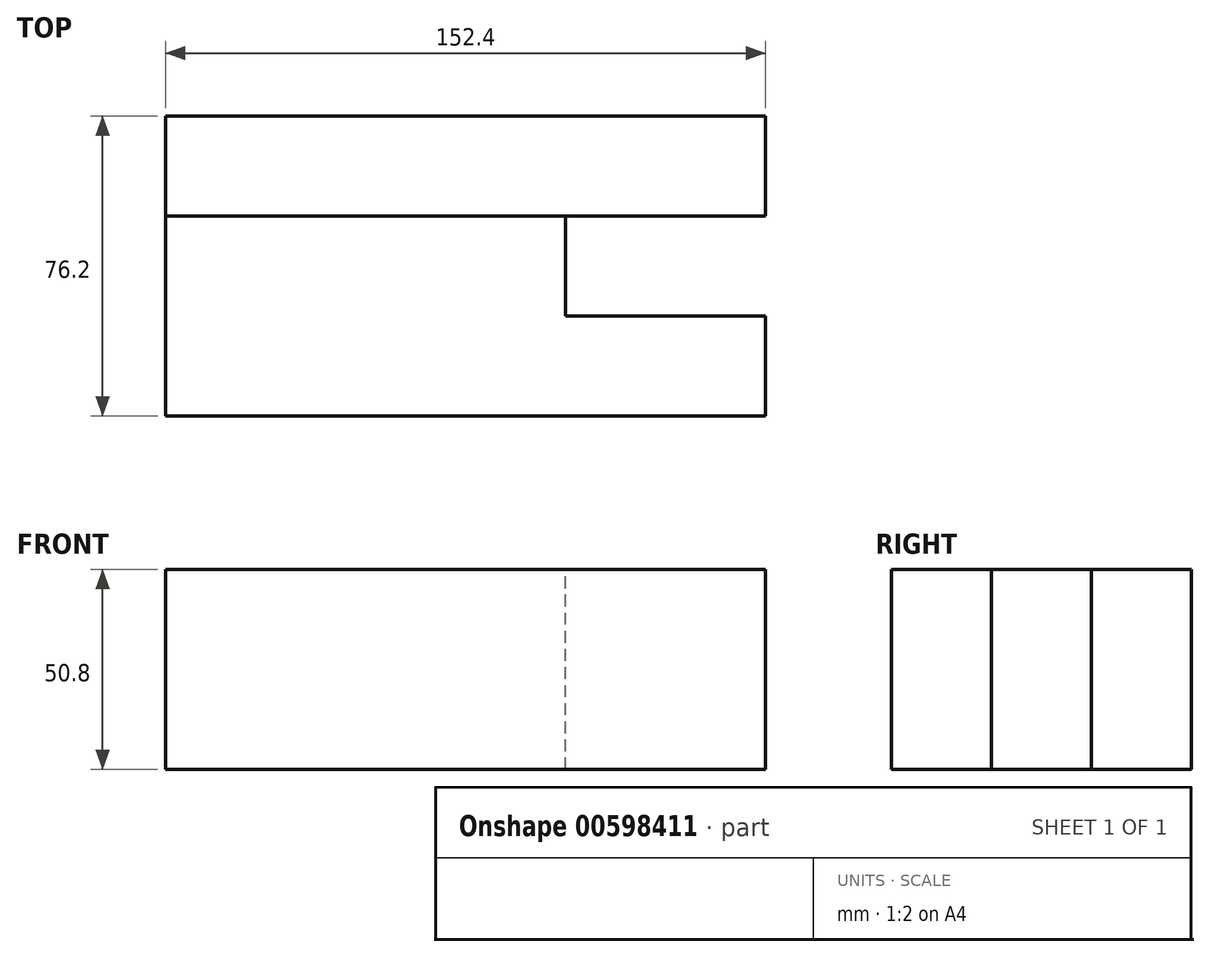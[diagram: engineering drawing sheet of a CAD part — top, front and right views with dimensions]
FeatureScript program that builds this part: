
annotation { "Feature Type Name" : "Feature", "Feature Type Description" : "" }
export const myFeature = defineFeature(function(context is Context, id is Id, definition is map)
    precondition{}
    {
        {
            var Q0;
            Q0=qCreatedBy(makeId("Front.planeOp"),FACE);
            var sketch = newSketch(context, id + "F0", { "sketchPlane" : qUnion([Q0])});
            skLineSegment(sketch, "E0", {"start": v(0, 0) * mm, "end": v(0, 50.8) * mm});
            skLineSegment(sketch, "E1", {"start": v(0, 50.8) * mm, "end": v(152.4, 50.8) * mm});
            skLineSegment(sketch, "E2", {"start": v(0, 0) * mm, "end": v(152.4, 0) * mm});
            skLineSegment(sketch, "E3", {"start": v(152.4, 50.8) * mm, "end": v(152.4, 0) * mm});
            skSolve(sketch);
        }
        {
            var Q0;
            Q0 = qSketchRegion(id + "F0", true);
            extrude(context, id + "F1", {"entities" : qUnion([Q0]), "depth" : 25.4 * mm, "offsetDistance" : 25.4 * mm});
        }
        {
            var Q0;
            Q0=qCreatedBy(makeId("Right.planeOp"),FACE);
            var sketch = newSketch(context, id + "F2", { "sketchPlane" : qUnion([Q0])});
            skLineSegment(sketch, "E4", {"start": v(0, 0) * mm, "end": v(0, 50.8) * mm});
            skLineSegment(sketch, "E5", {"start": v(0, 50.8) * mm, "end": v(25.4, 50.8) * mm});
            skLineSegment(sketch, "E6", {"start": v(25.4, 50.8) * mm, "end": v(25.4, 0) * mm});
            skLineSegment(sketch, "E7", {"start": v(25.4, 0) * mm, "end": v(0, 0) * mm});
            skSolve(sketch);
        }
        {
            var Q0;
            Q0 = qSketchRegion(id + "F2", true);
            extrude(context, id + "F3", {"entities" : qUnion([Q0]), "operationType" : NewBodyOperationType.ADD, "depth" : 101.6 * mm, "offsetDistance" : 25.4 * mm});
        }
        {
            var Q0;
            Q0=qCreatedBy(makeId("Right.planeOp"),FACE);
            var sketch = newSketch(context, id + "F4", { "sketchPlane" : qUnion([Q0])});
            skLineSegment(sketch, "E8", {"start": v(25.4, 0) * mm, "end": v(50.8, 0) * mm});
            skLineSegment(sketch, "E9", {"start": v(50.8, 0) * mm, "end": v(50.8, 50.8) * mm});
            skLineSegment(sketch, "E10", {"start": v(50.8, 50.8) * mm, "end": v(25.4, 50.8) * mm});
            skLineSegment(sketch, "E11", {"start": v(25.4, 50.8) * mm, "end": v(25.4, 0) * mm});
            skSolve(sketch);
        }
        {
            var Q0;
            Q0 = qSketchRegion(id + "F4", true);
            extrude(context, id + "F5", {"entities" : qUnion([Q0]), "depth" : 152.4 * mm, "offsetDistance" : 25.4 * mm});
        }
    });
